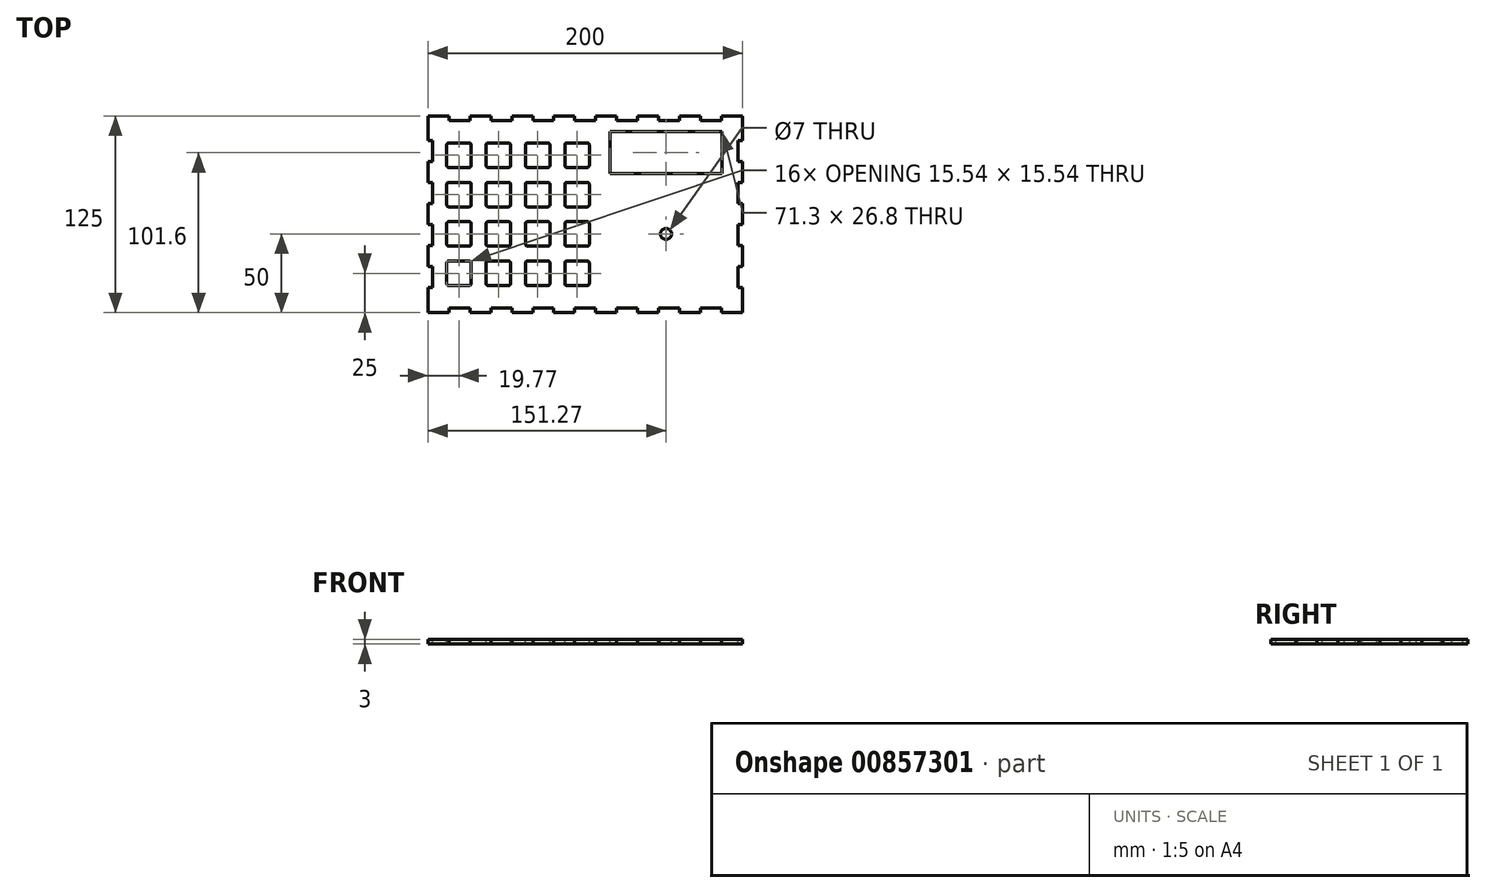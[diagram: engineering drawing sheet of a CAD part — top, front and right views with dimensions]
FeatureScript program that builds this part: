
annotation { "Feature Type Name" : "Feature", "Feature Type Description" : "" }
export const myFeature = defineFeature(function(context is Context, id is Id, definition is map)
    precondition{}
    {
        {
            var Q0;
            Q0=qCreatedBy(makeId("Top.planeOp"),FACE);
            var sketch = newSketch(context, id + "F0", { "sketchPlane" : qUnion([Q0])});
            skLineSegment(sketch, "E0.bottom", {"start": v(100, -62.5) * mm, "end": v(-100, -62.5) * mm});
            skLineSegment(sketch, "E0.top", {"start": v(100, 62.5) * mm, "end": v(-100, 62.5) * mm});
            skLineSegment(sketch, "E0.left", {"start": v(100, -62.5) * mm, "end": v(100, 62.5) * mm});
            skLineSegment(sketch, "E0.right", {"start": v(-100, -62.5) * mm, "end": v(-100, 62.5) * mm});
            skPoint(sketch, "E0.middle", {"position": v(0, 0) * mm});
            skSolve(sketch);
        }
        {
            var Q0;
            Q0=makeQuery(id+"F0.imprint","IMPRINT",FACE,{"disambiguationData":[TD([[makeQuery(id+"F0.imprint","IMPRINT",EDGE,{"derivedFrom":sQuery(id+"F0.wireOp",EDGE,"E0.bottom")}),-1.0]])]});
            extrude(context, id + "F1", {"entities" : qUnion([Q0]), "depth" : 3 * mm, "offsetDistance" : 25 * mm});
        }
        {
            var Q0;
            Q0=makeQuery(id+"F1.opExtrude","CAP_FACE",FACE,{"disambiguationData":[OSD([sQuery(id+"F0.wireOp",EDGE,"E0.bottom"),sQuery(id+"F0.wireOp",EDGE,"E0.top"),sQuery(id+"F0.wireOp",EDGE,"E0.left"),sQuery(id+"F0.wireOp",EDGE,"E0.right")])],"isStart":false});
            var sketch = newSketch(context, id + "F2", { "sketchPlane" : qUnion([Q0])});
            skLineSegment(sketch, "E1.bottom", {"start": v(-73.7, -45.27) * mm, "end": v(-86.75, -45.27) * mm});
            skLineSegment(sketch, "E1.top", {"start": v(-73.7, -29.73) * mm, "end": v(-86.75, -29.73) * mm});
            skLineSegment(sketch, "E1.left", {"start": v(-72.46, -44.02) * mm, "end": v(-72.46, -30.98) * mm});
            skLineSegment(sketch, "E1.right", {"start": v(-88, -44.02) * mm, "end": v(-88, -30.98) * mm});
            skPoint(sketch, "E1.middle", {"position": v(-80.23, -37.5) * mm});
            skPoint(sketch, "E2.visualSharp", {"position": v(-88, -29.73) * mm});
            skArc(sketch, "E2.filletArc", {"start": v(-86.75, -29.73) * mm, "mid": v(-87.63, -30.1) * mm, "end": v(-88, -30.98) * mm});
            skPoint(sketch, "E3.visualSharp", {"position": v(-72.46, -29.73) * mm});
            skArc(sketch, "E3.filletArc", {"start": v(-72.46, -30.98) * mm, "mid": v(-72.83, -30.1) * mm, "end": v(-73.7, -29.73) * mm});
            skPoint(sketch, "E4.visualSharp", {"position": v(-72.46, -45.27) * mm});
            skArc(sketch, "E4.filletArc", {"start": v(-73.7, -45.27) * mm, "mid": v(-72.83, -44.9) * mm, "end": v(-72.46, -44.02) * mm});
            skPoint(sketch, "E5.visualSharp", {"position": v(-88, -45.27) * mm});
            skArc(sketch, "E5.filletArc", {"start": v(-88, -44.02) * mm, "mid": v(-87.63, -44.9) * mm, "end": v(-86.75, -45.27) * mm});
            skLineSegment(sketch, "E6.0.1.0", {"start": v(-73.7, -4.73) * mm, "end": v(-86.75, -4.73) * mm});
            skPoint(sketch, "E6.0.1.1", {"position": v(-80.23, -12.5) * mm});
            skPoint(sketch, "E6.0.1.2", {"position": v(-72.46, -4.73) * mm});
            skLineSegment(sketch, "E6.0.1.3", {"start": v(-72.46, -19.02) * mm, "end": v(-72.46, -5.98) * mm});
            skLineSegment(sketch, "E6.0.1.4", {"start": v(-88, -19.02) * mm, "end": v(-88, -5.98) * mm});
            skPoint(sketch, "E6.0.1.5", {"position": v(-72.46, -20.27) * mm});
            skLineSegment(sketch, "E6.0.1.6", {"start": v(-73.7, -20.27) * mm, "end": v(-86.75, -20.27) * mm});
            skPoint(sketch, "E6.0.1.7", {"position": v(-88, -20.27) * mm});
            skPoint(sketch, "E6.0.1.8", {"position": v(-88, -4.73) * mm});
            skArc(sketch, "E6.0.1.9", {"start": v(-73.7, -20.27) * mm, "mid": v(-72.83, -19.9) * mm, "end": v(-72.46, -19.02) * mm});
            skArc(sketch, "E6.0.1.10", {"start": v(-88, -19.02) * mm, "mid": v(-87.63, -19.9) * mm, "end": v(-86.75, -20.27) * mm});
            skArc(sketch, "E6.0.1.11", {"start": v(-86.75, -4.73) * mm, "mid": v(-87.63, -5.1) * mm, "end": v(-88, -5.98) * mm});
            skArc(sketch, "E6.0.1.12", {"start": v(-72.46, -5.98) * mm, "mid": v(-72.83, -5.1) * mm, "end": v(-73.7, -4.73) * mm});
            skLineSegment(sketch, "E6.0.2.0", {"start": v(-73.7, 20.27) * mm, "end": v(-86.75, 20.27) * mm});
            skPoint(sketch, "E6.0.2.1", {"position": v(-80.23, 12.5) * mm});
            skPoint(sketch, "E6.0.2.2", {"position": v(-72.46, 20.27) * mm});
            skLineSegment(sketch, "E6.0.2.3", {"start": v(-72.46, 5.98) * mm, "end": v(-72.46, 19.02) * mm});
            skLineSegment(sketch, "E6.0.2.4", {"start": v(-88, 5.98) * mm, "end": v(-88, 19.02) * mm});
            skPoint(sketch, "E6.0.2.5", {"position": v(-72.46, 4.73) * mm});
            skLineSegment(sketch, "E6.0.2.6", {"start": v(-73.7, 4.73) * mm, "end": v(-86.75, 4.73) * mm});
            skPoint(sketch, "E6.0.2.7", {"position": v(-88, 4.73) * mm});
            skPoint(sketch, "E6.0.2.8", {"position": v(-88, 20.27) * mm});
            skArc(sketch, "E6.0.2.9", {"start": v(-73.7, 4.73) * mm, "mid": v(-72.83, 5.1) * mm, "end": v(-72.46, 5.98) * mm});
            skArc(sketch, "E6.0.2.10", {"start": v(-88, 5.98) * mm, "mid": v(-87.63, 5.1) * mm, "end": v(-86.75, 4.73) * mm});
            skArc(sketch, "E6.0.2.11", {"start": v(-86.75, 20.27) * mm, "mid": v(-87.63, 19.9) * mm, "end": v(-88, 19.02) * mm});
            skArc(sketch, "E6.0.2.12", {"start": v(-72.46, 19.02) * mm, "mid": v(-72.83, 19.9) * mm, "end": v(-73.7, 20.27) * mm});
            skLineSegment(sketch, "E6.0.3.0", {"start": v(-73.71, 45.27) * mm, "end": v(-86.75, 45.27) * mm});
            skPoint(sketch, "E6.0.3.1", {"position": v(-80.23, 37.5) * mm});
            skPoint(sketch, "E6.0.3.2", {"position": v(-72.46, 45.27) * mm});
            skLineSegment(sketch, "E6.0.3.3", {"start": v(-72.46, 30.98) * mm, "end": v(-72.46, 44.02) * mm});
            skLineSegment(sketch, "E6.0.3.4", {"start": v(-88, 30.98) * mm, "end": v(-88, 44.02) * mm});
            skPoint(sketch, "E6.0.3.5", {"position": v(-72.46, 29.73) * mm});
            skLineSegment(sketch, "E6.0.3.6", {"start": v(-73.71, 29.73) * mm, "end": v(-86.75, 29.73) * mm});
            skPoint(sketch, "E6.0.3.7", {"position": v(-88, 29.73) * mm});
            skPoint(sketch, "E6.0.3.8", {"position": v(-88, 45.27) * mm});
            skArc(sketch, "E6.0.3.9", {"start": v(-73.71, 29.73) * mm, "mid": v(-72.83, 30.1) * mm, "end": v(-72.46, 30.98) * mm});
            skArc(sketch, "E6.0.3.10", {"start": v(-88, 30.98) * mm, "mid": v(-87.63, 30.1) * mm, "end": v(-86.75, 29.73) * mm});
            skArc(sketch, "E6.0.3.11", {"start": v(-86.75, 45.27) * mm, "mid": v(-87.63, 44.9) * mm, "end": v(-88, 44.02) * mm});
            skArc(sketch, "E6.0.3.12", {"start": v(-72.46, 44.02) * mm, "mid": v(-72.83, 44.9) * mm, "end": v(-73.71, 45.27) * mm});
            skLineSegment(sketch, "E6.1.0.0", {"start": v(-48.71, -29.73) * mm, "end": v(-61.75, -29.73) * mm});
            skPoint(sketch, "E6.1.0.1", {"position": v(-55.23, -37.5) * mm});
            skPoint(sketch, "E6.1.0.2", {"position": v(-47.46, -29.73) * mm});
            skLineSegment(sketch, "E6.1.0.3", {"start": v(-47.46, -44.02) * mm, "end": v(-47.46, -30.98) * mm});
            skLineSegment(sketch, "E6.1.0.4", {"start": v(-63, -44.02) * mm, "end": v(-63, -30.98) * mm});
            skPoint(sketch, "E6.1.0.5", {"position": v(-47.46, -45.27) * mm});
            skLineSegment(sketch, "E6.1.0.6", {"start": v(-48.71, -45.27) * mm, "end": v(-61.75, -45.27) * mm});
            skPoint(sketch, "E6.1.0.7", {"position": v(-63, -45.27) * mm});
            skPoint(sketch, "E6.1.0.8", {"position": v(-63, -29.73) * mm});
            skArc(sketch, "E6.1.0.9", {"start": v(-48.71, -45.27) * mm, "mid": v(-47.83, -44.9) * mm, "end": v(-47.46, -44.02) * mm});
            skArc(sketch, "E6.1.0.10", {"start": v(-63, -44.02) * mm, "mid": v(-62.63, -44.9) * mm, "end": v(-61.75, -45.27) * mm});
            skArc(sketch, "E6.1.0.11", {"start": v(-61.75, -29.73) * mm, "mid": v(-62.63, -30.1) * mm, "end": v(-63, -30.98) * mm});
            skArc(sketch, "E6.1.0.12", {"start": v(-47.46, -30.98) * mm, "mid": v(-47.83, -30.1) * mm, "end": v(-48.71, -29.73) * mm});
            skLineSegment(sketch, "E6.1.1.0", {"start": v(-48.71, -4.73) * mm, "end": v(-61.75, -4.73) * mm});
            skPoint(sketch, "E6.1.1.1", {"position": v(-55.23, -12.5) * mm});
            skPoint(sketch, "E6.1.1.2", {"position": v(-47.46, -4.73) * mm});
            skLineSegment(sketch, "E6.1.1.3", {"start": v(-47.46, -19.02) * mm, "end": v(-47.46, -5.98) * mm});
            skLineSegment(sketch, "E6.1.1.4", {"start": v(-63, -19.02) * mm, "end": v(-63, -5.98) * mm});
            skPoint(sketch, "E6.1.1.5", {"position": v(-47.46, -20.27) * mm});
            skLineSegment(sketch, "E6.1.1.6", {"start": v(-48.71, -20.27) * mm, "end": v(-61.75, -20.27) * mm});
            skPoint(sketch, "E6.1.1.7", {"position": v(-63, -20.27) * mm});
            skPoint(sketch, "E6.1.1.8", {"position": v(-63, -4.73) * mm});
            skArc(sketch, "E6.1.1.9", {"start": v(-48.71, -20.27) * mm, "mid": v(-47.83, -19.9) * mm, "end": v(-47.46, -19.02) * mm});
            skArc(sketch, "E6.1.1.10", {"start": v(-63, -19.02) * mm, "mid": v(-62.63, -19.9) * mm, "end": v(-61.75, -20.27) * mm});
            skArc(sketch, "E6.1.1.11", {"start": v(-61.75, -4.73) * mm, "mid": v(-62.63, -5.1) * mm, "end": v(-63, -5.98) * mm});
            skArc(sketch, "E6.1.1.12", {"start": v(-47.46, -5.98) * mm, "mid": v(-47.83, -5.1) * mm, "end": v(-48.71, -4.73) * mm});
            skLineSegment(sketch, "E6.1.2.0", {"start": v(-48.71, 20.27) * mm, "end": v(-61.75, 20.27) * mm});
            skPoint(sketch, "E6.1.2.1", {"position": v(-55.23, 12.5) * mm});
            skPoint(sketch, "E6.1.2.2", {"position": v(-47.46, 20.27) * mm});
            skLineSegment(sketch, "E6.1.2.3", {"start": v(-47.46, 5.98) * mm, "end": v(-47.46, 19.02) * mm});
            skLineSegment(sketch, "E6.1.2.4", {"start": v(-63, 5.98) * mm, "end": v(-63, 19.02) * mm});
            skPoint(sketch, "E6.1.2.5", {"position": v(-47.46, 4.73) * mm});
            skLineSegment(sketch, "E6.1.2.6", {"start": v(-48.71, 4.73) * mm, "end": v(-61.75, 4.73) * mm});
            skPoint(sketch, "E6.1.2.7", {"position": v(-63, 4.73) * mm});
            skPoint(sketch, "E6.1.2.8", {"position": v(-63, 20.27) * mm});
            skArc(sketch, "E6.1.2.9", {"start": v(-48.71, 4.73) * mm, "mid": v(-47.83, 5.1) * mm, "end": v(-47.46, 5.98) * mm});
            skArc(sketch, "E6.1.2.10", {"start": v(-63, 5.98) * mm, "mid": v(-62.63, 5.1) * mm, "end": v(-61.75, 4.73) * mm});
            skArc(sketch, "E6.1.2.11", {"start": v(-61.75, 20.27) * mm, "mid": v(-62.63, 19.9) * mm, "end": v(-63, 19.02) * mm});
            skArc(sketch, "E6.1.2.12", {"start": v(-47.46, 19.02) * mm, "mid": v(-47.83, 19.9) * mm, "end": v(-48.71, 20.27) * mm});
            skLineSegment(sketch, "E6.1.3.0", {"start": v(-48.71, 45.27) * mm, "end": v(-61.75, 45.27) * mm});
            skPoint(sketch, "E6.1.3.1", {"position": v(-55.23, 37.5) * mm});
            skPoint(sketch, "E6.1.3.2", {"position": v(-47.46, 45.27) * mm});
            skLineSegment(sketch, "E6.1.3.3", {"start": v(-47.46, 30.98) * mm, "end": v(-47.46, 44.02) * mm});
            skLineSegment(sketch, "E6.1.3.4", {"start": v(-63, 30.98) * mm, "end": v(-63, 44.02) * mm});
            skPoint(sketch, "E6.1.3.5", {"position": v(-47.46, 29.73) * mm});
            skLineSegment(sketch, "E6.1.3.6", {"start": v(-48.71, 29.73) * mm, "end": v(-61.75, 29.73) * mm});
            skPoint(sketch, "E6.1.3.7", {"position": v(-63, 29.73) * mm});
            skPoint(sketch, "E6.1.3.8", {"position": v(-63, 45.27) * mm});
            skArc(sketch, "E6.1.3.9", {"start": v(-48.71, 29.73) * mm, "mid": v(-47.83, 30.1) * mm, "end": v(-47.46, 30.98) * mm});
            skArc(sketch, "E6.1.3.10", {"start": v(-63, 30.98) * mm, "mid": v(-62.63, 30.1) * mm, "end": v(-61.75, 29.73) * mm});
            skArc(sketch, "E6.1.3.11", {"start": v(-61.75, 45.27) * mm, "mid": v(-62.63, 44.9) * mm, "end": v(-63, 44.02) * mm});
            skArc(sketch, "E6.1.3.12", {"start": v(-47.46, 44.02) * mm, "mid": v(-47.83, 44.9) * mm, "end": v(-48.71, 45.27) * mm});
            skLineSegment(sketch, "E6.2.0.0", {"start": v(-23.71, -29.73) * mm, "end": v(-36.75, -29.73) * mm});
            skPoint(sketch, "E6.2.0.1", {"position": v(-30.23, -37.5) * mm});
            skPoint(sketch, "E6.2.0.2", {"position": v(-22.46, -29.73) * mm});
            skLineSegment(sketch, "E6.2.0.3", {"start": v(-22.46, -44.02) * mm, "end": v(-22.46, -30.98) * mm});
            skLineSegment(sketch, "E6.2.0.4", {"start": v(-38, -44.02) * mm, "end": v(-38, -30.98) * mm});
            skPoint(sketch, "E6.2.0.5", {"position": v(-22.46, -45.27) * mm});
            skLineSegment(sketch, "E6.2.0.6", {"start": v(-23.71, -45.27) * mm, "end": v(-36.75, -45.27) * mm});
            skPoint(sketch, "E6.2.0.7", {"position": v(-38, -45.27) * mm});
            skPoint(sketch, "E6.2.0.8", {"position": v(-38, -29.73) * mm});
            skArc(sketch, "E6.2.0.9", {"start": v(-23.71, -45.27) * mm, "mid": v(-22.83, -44.9) * mm, "end": v(-22.46, -44.02) * mm});
            skArc(sketch, "E6.2.0.10", {"start": v(-38, -44.02) * mm, "mid": v(-37.63, -44.9) * mm, "end": v(-36.75, -45.27) * mm});
            skArc(sketch, "E6.2.0.11", {"start": v(-36.75, -29.73) * mm, "mid": v(-37.63, -30.1) * mm, "end": v(-38, -30.98) * mm});
            skArc(sketch, "E6.2.0.12", {"start": v(-22.46, -30.98) * mm, "mid": v(-22.83, -30.1) * mm, "end": v(-23.71, -29.73) * mm});
            skLineSegment(sketch, "E6.2.1.0", {"start": v(-23.71, -4.73) * mm, "end": v(-36.75, -4.73) * mm});
            skPoint(sketch, "E6.2.1.1", {"position": v(-30.23, -12.5) * mm});
            skPoint(sketch, "E6.2.1.2", {"position": v(-22.46, -4.73) * mm});
            skLineSegment(sketch, "E6.2.1.3", {"start": v(-22.46, -19.02) * mm, "end": v(-22.46, -5.98) * mm});
            skLineSegment(sketch, "E6.2.1.4", {"start": v(-38, -19.02) * mm, "end": v(-38, -5.98) * mm});
            skPoint(sketch, "E6.2.1.5", {"position": v(-22.46, -20.27) * mm});
            skLineSegment(sketch, "E6.2.1.6", {"start": v(-23.71, -20.27) * mm, "end": v(-36.75, -20.27) * mm});
            skPoint(sketch, "E6.2.1.7", {"position": v(-38, -20.27) * mm});
            skPoint(sketch, "E6.2.1.8", {"position": v(-38, -4.73) * mm});
            skArc(sketch, "E6.2.1.9", {"start": v(-23.71, -20.27) * mm, "mid": v(-22.83, -19.9) * mm, "end": v(-22.46, -19.02) * mm});
            skArc(sketch, "E6.2.1.10", {"start": v(-38, -19.02) * mm, "mid": v(-37.63, -19.9) * mm, "end": v(-36.75, -20.27) * mm});
            skArc(sketch, "E6.2.1.11", {"start": v(-36.75, -4.73) * mm, "mid": v(-37.63, -5.1) * mm, "end": v(-38, -5.98) * mm});
            skArc(sketch, "E6.2.1.12", {"start": v(-22.46, -5.98) * mm, "mid": v(-22.83, -5.1) * mm, "end": v(-23.71, -4.73) * mm});
            skLineSegment(sketch, "E6.2.2.0", {"start": v(-23.71, 20.27) * mm, "end": v(-36.75, 20.27) * mm});
            skPoint(sketch, "E6.2.2.1", {"position": v(-30.23, 12.5) * mm});
            skPoint(sketch, "E6.2.2.2", {"position": v(-22.46, 20.27) * mm});
            skLineSegment(sketch, "E6.2.2.3", {"start": v(-22.46, 5.98) * mm, "end": v(-22.46, 19.02) * mm});
            skLineSegment(sketch, "E6.2.2.4", {"start": v(-38, 5.98) * mm, "end": v(-38, 19.02) * mm});
            skPoint(sketch, "E6.2.2.5", {"position": v(-22.46, 4.73) * mm});
            skLineSegment(sketch, "E6.2.2.6", {"start": v(-23.71, 4.73) * mm, "end": v(-36.75, 4.73) * mm});
            skPoint(sketch, "E6.2.2.7", {"position": v(-38, 4.73) * mm});
            skPoint(sketch, "E6.2.2.8", {"position": v(-38, 20.27) * mm});
            skArc(sketch, "E6.2.2.9", {"start": v(-23.71, 4.73) * mm, "mid": v(-22.83, 5.1) * mm, "end": v(-22.46, 5.98) * mm});
            skArc(sketch, "E6.2.2.10", {"start": v(-38, 5.98) * mm, "mid": v(-37.63, 5.1) * mm, "end": v(-36.75, 4.73) * mm});
            skArc(sketch, "E6.2.2.11", {"start": v(-36.75, 20.27) * mm, "mid": v(-37.63, 19.9) * mm, "end": v(-38, 19.02) * mm});
            skArc(sketch, "E6.2.2.12", {"start": v(-22.46, 19.02) * mm, "mid": v(-22.83, 19.9) * mm, "end": v(-23.71, 20.27) * mm});
            skLineSegment(sketch, "E6.2.3.0", {"start": v(-23.71, 45.27) * mm, "end": v(-36.75, 45.27) * mm});
            skPoint(sketch, "E6.2.3.1", {"position": v(-30.23, 37.5) * mm});
            skPoint(sketch, "E6.2.3.2", {"position": v(-22.46, 45.27) * mm});
            skLineSegment(sketch, "E6.2.3.3", {"start": v(-22.46, 30.98) * mm, "end": v(-22.46, 44.02) * mm});
            skLineSegment(sketch, "E6.2.3.4", {"start": v(-38, 30.98) * mm, "end": v(-38, 44.02) * mm});
            skPoint(sketch, "E6.2.3.5", {"position": v(-22.46, 29.73) * mm});
            skLineSegment(sketch, "E6.2.3.6", {"start": v(-23.71, 29.73) * mm, "end": v(-36.75, 29.73) * mm});
            skPoint(sketch, "E6.2.3.7", {"position": v(-38, 29.73) * mm});
            skPoint(sketch, "E6.2.3.8", {"position": v(-38, 45.27) * mm});
            skArc(sketch, "E6.2.3.9", {"start": v(-23.71, 29.73) * mm, "mid": v(-22.83, 30.1) * mm, "end": v(-22.46, 30.98) * mm});
            skArc(sketch, "E6.2.3.10", {"start": v(-38, 30.98) * mm, "mid": v(-37.63, 30.1) * mm, "end": v(-36.75, 29.73) * mm});
            skArc(sketch, "E6.2.3.11", {"start": v(-36.75, 45.27) * mm, "mid": v(-37.63, 44.9) * mm, "end": v(-38, 44.02) * mm});
            skArc(sketch, "E6.2.3.12", {"start": v(-22.46, 44.02) * mm, "mid": v(-22.83, 44.9) * mm, "end": v(-23.71, 45.27) * mm});
            skLineSegment(sketch, "E6.3.0.0", {"start": v(1.29, -29.73) * mm, "end": v(-11.75, -29.73) * mm});
            skPoint(sketch, "E6.3.0.1", {"position": v(-5.23, -37.5) * mm});
            skPoint(sketch, "E6.3.0.2", {"position": v(2.54, -29.73) * mm});
            skLineSegment(sketch, "E6.3.0.3", {"start": v(2.54, -44.02) * mm, "end": v(2.54, -30.98) * mm});
            skLineSegment(sketch, "E6.3.0.4", {"start": v(-13, -44.02) * mm, "end": v(-13, -30.98) * mm});
            skPoint(sketch, "E6.3.0.5", {"position": v(2.54, -45.27) * mm});
            skLineSegment(sketch, "E6.3.0.6", {"start": v(1.29, -45.27) * mm, "end": v(-11.75, -45.27) * mm});
            skPoint(sketch, "E6.3.0.7", {"position": v(-13, -45.27) * mm});
            skPoint(sketch, "E6.3.0.8", {"position": v(-13, -29.73) * mm});
            skArc(sketch, "E6.3.0.9", {"start": v(1.29, -45.27) * mm, "mid": v(2.17, -44.9) * mm, "end": v(2.54, -44.02) * mm});
            skArc(sketch, "E6.3.0.10", {"start": v(-13, -44.02) * mm, "mid": v(-12.63, -44.9) * mm, "end": v(-11.75, -45.27) * mm});
            skArc(sketch, "E6.3.0.11", {"start": v(-11.75, -29.73) * mm, "mid": v(-12.63, -30.1) * mm, "end": v(-13, -30.98) * mm});
            skArc(sketch, "E6.3.0.12", {"start": v(2.54, -30.98) * mm, "mid": v(2.17, -30.1) * mm, "end": v(1.29, -29.73) * mm});
            skLineSegment(sketch, "E6.3.1.0", {"start": v(1.29, -4.73) * mm, "end": v(-11.75, -4.73) * mm});
            skPoint(sketch, "E6.3.1.1", {"position": v(-5.23, -12.5) * mm});
            skPoint(sketch, "E6.3.1.2", {"position": v(2.54, -4.73) * mm});
            skLineSegment(sketch, "E6.3.1.3", {"start": v(2.54, -19.02) * mm, "end": v(2.54, -5.98) * mm});
            skLineSegment(sketch, "E6.3.1.4", {"start": v(-13, -19.02) * mm, "end": v(-13, -5.98) * mm});
            skPoint(sketch, "E6.3.1.5", {"position": v(2.54, -20.27) * mm});
            skLineSegment(sketch, "E6.3.1.6", {"start": v(1.29, -20.27) * mm, "end": v(-11.75, -20.27) * mm});
            skPoint(sketch, "E6.3.1.7", {"position": v(-13, -20.27) * mm});
            skPoint(sketch, "E6.3.1.8", {"position": v(-13, -4.73) * mm});
            skArc(sketch, "E6.3.1.9", {"start": v(1.29, -20.27) * mm, "mid": v(2.17, -19.9) * mm, "end": v(2.54, -19.02) * mm});
            skArc(sketch, "E6.3.1.10", {"start": v(-13, -19.02) * mm, "mid": v(-12.63, -19.9) * mm, "end": v(-11.75, -20.27) * mm});
            skArc(sketch, "E6.3.1.11", {"start": v(-11.75, -4.73) * mm, "mid": v(-12.63, -5.1) * mm, "end": v(-13, -5.98) * mm});
            skArc(sketch, "E6.3.1.12", {"start": v(2.54, -5.98) * mm, "mid": v(2.17, -5.1) * mm, "end": v(1.29, -4.73) * mm});
            skLineSegment(sketch, "E6.3.2.0", {"start": v(1.29, 20.27) * mm, "end": v(-11.75, 20.27) * mm});
            skPoint(sketch, "E6.3.2.1", {"position": v(-5.23, 12.5) * mm});
            skPoint(sketch, "E6.3.2.2", {"position": v(2.54, 20.27) * mm});
            skLineSegment(sketch, "E6.3.2.3", {"start": v(2.54, 5.98) * mm, "end": v(2.54, 19.02) * mm});
            skLineSegment(sketch, "E6.3.2.4", {"start": v(-13, 5.98) * mm, "end": v(-13, 19.02) * mm});
            skPoint(sketch, "E6.3.2.5", {"position": v(2.54, 4.73) * mm});
            skLineSegment(sketch, "E6.3.2.6", {"start": v(1.29, 4.73) * mm, "end": v(-11.75, 4.73) * mm});
            skPoint(sketch, "E6.3.2.7", {"position": v(-13, 4.73) * mm});
            skPoint(sketch, "E6.3.2.8", {"position": v(-13, 20.27) * mm});
            skArc(sketch, "E6.3.2.9", {"start": v(1.29, 4.73) * mm, "mid": v(2.17, 5.1) * mm, "end": v(2.54, 5.98) * mm});
            skArc(sketch, "E6.3.2.10", {"start": v(-13, 5.98) * mm, "mid": v(-12.63, 5.1) * mm, "end": v(-11.75, 4.73) * mm});
            skArc(sketch, "E6.3.2.11", {"start": v(-11.75, 20.27) * mm, "mid": v(-12.63, 19.9) * mm, "end": v(-13, 19.02) * mm});
            skArc(sketch, "E6.3.2.12", {"start": v(2.54, 19.02) * mm, "mid": v(2.17, 19.9) * mm, "end": v(1.29, 20.27) * mm});
            skLineSegment(sketch, "E6.3.3.0", {"start": v(1.29, 45.27) * mm, "end": v(-11.75, 45.27) * mm});
            skPoint(sketch, "E6.3.3.1", {"position": v(-5.23, 37.5) * mm});
            skPoint(sketch, "E6.3.3.2", {"position": v(2.54, 45.27) * mm});
            skLineSegment(sketch, "E6.3.3.3", {"start": v(2.54, 30.98) * mm, "end": v(2.54, 44.02) * mm});
            skLineSegment(sketch, "E6.3.3.4", {"start": v(-13, 30.98) * mm, "end": v(-13, 44.02) * mm});
            skPoint(sketch, "E6.3.3.5", {"position": v(2.54, 29.73) * mm});
            skLineSegment(sketch, "E6.3.3.6", {"start": v(1.29, 29.73) * mm, "end": v(-11.75, 29.73) * mm});
            skPoint(sketch, "E6.3.3.7", {"position": v(-13, 29.73) * mm});
            skPoint(sketch, "E6.3.3.8", {"position": v(-13, 45.27) * mm});
            skArc(sketch, "E6.3.3.9", {"start": v(1.29, 29.73) * mm, "mid": v(2.17, 30.1) * mm, "end": v(2.54, 30.98) * mm});
            skArc(sketch, "E6.3.3.10", {"start": v(-13, 30.98) * mm, "mid": v(-12.63, 30.1) * mm, "end": v(-11.75, 29.73) * mm});
            skArc(sketch, "E6.3.3.11", {"start": v(-11.75, 45.27) * mm, "mid": v(-12.63, 44.9) * mm, "end": v(-13, 44.02) * mm});
            skArc(sketch, "E6.3.3.12", {"start": v(2.54, 44.02) * mm, "mid": v(2.17, 44.9) * mm, "end": v(1.29, 45.27) * mm});
            skLineSegment(sketch, "E6.direction1", {"start": v(-88, -45.27) * mm, "end": v(-63, -45.27) * mm, "construction": true});
            skLineSegment(sketch, "E6.direction2", {"start": v(-88, -45.27) * mm, "end": v(-88, -20.27) * mm, "construction": true});
            skSolve(sketch);
        }
        {
            var Q0;
            Q0 = qSketchRegion(id + "F2", true);
            extrude(context, id + "F3", {"entities" : qUnion([Q0]), "operationType" : NewBodyOperationType.REMOVE, "endBound" : BoundingType.THROUGH_ALL, "oppositeDirection" : true, "depth" : 25 * mm, "offsetDistance" : 25 * mm});
        }
        {
            var Q0;
            Q0=makeQuery(id+"F1.opExtrude","CAP_FACE",FACE,{"disambiguationData":[OSD([sQuery(id+"F0.wireOp",EDGE,"E0.bottom"),sQuery(id+"F0.wireOp",EDGE,"E0.top"),sQuery(id+"F0.wireOp",EDGE,"E0.left"),sQuery(id+"F0.wireOp",EDGE,"E0.right")])],"isStart":false});
            var sketch = newSketch(context, id + "F4", { "sketchPlane" : qUnion([Q0])});
            skLineSegment(sketch, "E7", {"start": v(-100, -12.5) * mm, "end": v(100, -12.5) * mm, "construction": true});
            skPoint(sketch, "E8.startSnap0", {"position": v(2.54, 37.5) * mm});
            skCircle(sketch, "E9", {"center": v(51.27, -12.5) * mm, "radius": 3.5 * mm});
            skSolve(sketch);
        }
        {
            var Q0;
            Q0 = qSketchRegion(id + "F4", true);
            extrude(context, id + "F5", {"entities" : qUnion([Q0]), "operationType" : NewBodyOperationType.REMOVE, "endBound" : BoundingType.THROUGH_ALL, "oppositeDirection" : true, "depth" : 25 * mm, "offsetDistance" : 25 * mm});
        }
        {
            var Q0;
            Q0=makeQuery(id+"F1.opExtrude","CAP_FACE",FACE,{"disambiguationData":[OSD([sQuery(id+"F0.wireOp",EDGE,"E0.bottom"),sQuery(id+"F0.wireOp",EDGE,"E0.top"),sQuery(id+"F0.wireOp",EDGE,"E0.left"),sQuery(id+"F0.wireOp",EDGE,"E0.right")])],"isStart":false});
            var sketch = newSketch(context, id + "F6", { "sketchPlane" : qUnion([Q0])});
            skCircle(sketch, "E10", {"center": v(51.27, -12.5) * mm, "radius": 27.5 * mm, "construction": true});
            skLineSegment(sketch, "E11", {"start": v(51.27, -12.5) * mm, "end": v(51.27, 62.5) * mm, "construction": true});
            skLineSegment(sketch, "E12.bottom", {"start": v(86.92, 25.7) * mm, "end": v(15.62, 25.7) * mm});
            skLineSegment(sketch, "E12.top", {"start": v(86.92, 52.5) * mm, "end": v(15.62, 52.5) * mm});
            skLineSegment(sketch, "E12.left", {"start": v(86.92, 25.7) * mm, "end": v(86.92, 52.5) * mm});
            skLineSegment(sketch, "E12.right", {"start": v(15.62, 25.7) * mm, "end": v(15.62, 52.5) * mm});
            skPoint(sketch, "E12.middle", {"position": v(51.27, 39.1) * mm});
            skLineSegment(sketch, "E13", {"start": v(-47.83, 5.1) * mm, "end": v(-35.87, -6.86) * mm, "construction": true});
            skLineSegment(sketch, "E14.bottom", {"start": v(8.15, -50.88) * mm, "end": v(-91.85, -50.88) * mm, "construction": true});
            skLineSegment(sketch, "E14.top", {"start": v(8.15, 49.12) * mm, "end": v(-91.85, 49.12) * mm, "construction": true});
            skLineSegment(sketch, "E14.left", {"start": v(8.15, -50.88) * mm, "end": v(8.15, 49.12) * mm, "construction": true});
            skLineSegment(sketch, "E14.right", {"start": v(-91.85, -50.88) * mm, "end": v(-91.85, 49.12) * mm, "construction": true});
            skPoint(sketch, "E14.middle", {"position": v(-41.85, -0.88) * mm});
            skSolve(sketch);
        }
        {
            var Q0;
            Q0 = qSketchRegion(id + "F6", true);
            extrude(context, id + "F7", {"entities" : qUnion([Q0]), "operationType" : NewBodyOperationType.REMOVE, "endBound" : BoundingType.THROUGH_ALL, "oppositeDirection" : true, "depth" : 25 * mm, "offsetDistance" : 25 * mm});
        }
        {
            var Q0;
            Q0=makeQuery(id+"F1.opExtrude","CAP_FACE",FACE,{"disambiguationData":[OSD([sQuery(id+"F0.wireOp",EDGE,"E0.bottom"),sQuery(id+"F0.wireOp",EDGE,"E0.top"),sQuery(id+"F0.wireOp",EDGE,"E0.left"),sQuery(id+"F0.wireOp",EDGE,"E0.right")])],"isStart":false});
            var sketch = newSketch(context, id + "F8", { "sketchPlane" : qUnion([Q0])});
            skLineSegment(sketch, "E15.bottom", {"start": v(-86.67, 62.5) * mm, "end": v(-73.33, 62.5) * mm});
            skLineSegment(sketch, "E15.top", {"start": v(-86.67, 59.5) * mm, "end": v(-73.33, 59.5) * mm});
            skLineSegment(sketch, "E15.left", {"start": v(-86.67, 62.5) * mm, "end": v(-86.67, 59.5) * mm});
            skLineSegment(sketch, "E15.right", {"start": v(-73.33, 62.5) * mm, "end": v(-73.33, 59.5) * mm});
            skLineSegment(sketch, "E16.1.0.0", {"start": v(-60, 62.5) * mm, "end": v(-46.67, 62.5) * mm});
            skLineSegment(sketch, "E16.1.0.1", {"start": v(-60, 62.5) * mm, "end": v(-60, 59.5) * mm});
            skLineSegment(sketch, "E16.1.0.2", {"start": v(-46.67, 62.5) * mm, "end": v(-46.67, 59.5) * mm});
            skLineSegment(sketch, "E16.1.0.3", {"start": v(-60, 59.5) * mm, "end": v(-46.67, 59.5) * mm});
            skLineSegment(sketch, "E16.2.0.0", {"start": v(-33.33, 62.5) * mm, "end": v(-20, 62.5) * mm});
            skLineSegment(sketch, "E16.2.0.1", {"start": v(-33.33, 62.5) * mm, "end": v(-33.33, 59.5) * mm});
            skLineSegment(sketch, "E16.2.0.2", {"start": v(-20, 62.5) * mm, "end": v(-20, 59.5) * mm});
            skLineSegment(sketch, "E16.2.0.3", {"start": v(-33.33, 59.5) * mm, "end": v(-20, 59.5) * mm});
            skLineSegment(sketch, "E16.3.0.0", {"start": v(-6.67, 62.5) * mm, "end": v(6.67, 62.5) * mm});
            skLineSegment(sketch, "E16.3.0.1", {"start": v(-6.67, 62.5) * mm, "end": v(-6.67, 59.5) * mm});
            skLineSegment(sketch, "E16.3.0.2", {"start": v(6.67, 62.5) * mm, "end": v(6.67, 59.5) * mm});
            skLineSegment(sketch, "E16.3.0.3", {"start": v(-6.67, 59.5) * mm, "end": v(6.67, 59.5) * mm});
            skLineSegment(sketch, "E16.4.0.0", {"start": v(20, 62.5) * mm, "end": v(33.33, 62.5) * mm});
            skLineSegment(sketch, "E16.4.0.1", {"start": v(20, 62.5) * mm, "end": v(20, 59.5) * mm});
            skLineSegment(sketch, "E16.4.0.2", {"start": v(33.33, 62.5) * mm, "end": v(33.33, 59.5) * mm});
            skLineSegment(sketch, "E16.4.0.3", {"start": v(20, 59.5) * mm, "end": v(33.33, 59.5) * mm});
            skLineSegment(sketch, "E16.5.0.0", {"start": v(46.67, 62.5) * mm, "end": v(60, 62.5) * mm});
            skLineSegment(sketch, "E16.5.0.1", {"start": v(46.67, 62.5) * mm, "end": v(46.67, 59.5) * mm});
            skLineSegment(sketch, "E16.5.0.2", {"start": v(60, 62.5) * mm, "end": v(60, 59.5) * mm});
            skLineSegment(sketch, "E16.5.0.3", {"start": v(46.67, 59.5) * mm, "end": v(60, 59.5) * mm});
            skLineSegment(sketch, "E16.6.0.0", {"start": v(73.33, 62.5) * mm, "end": v(86.67, 62.5) * mm});
            skLineSegment(sketch, "E16.6.0.1", {"start": v(73.33, 62.5) * mm, "end": v(73.33, 59.5) * mm});
            skLineSegment(sketch, "E16.6.0.2", {"start": v(86.67, 62.5) * mm, "end": v(86.67, 59.5) * mm});
            skLineSegment(sketch, "E16.6.0.3", {"start": v(73.33, 59.5) * mm, "end": v(86.67, 59.5) * mm});
            skLineSegment(sketch, "E17.bottom", {"start": v(-100, 46.66) * mm, "end": v(-97, 46.66) * mm});
            skLineSegment(sketch, "E17.top", {"start": v(-100, 33.33) * mm, "end": v(-97, 33.33) * mm});
            skLineSegment(sketch, "E17.left", {"start": v(-100, 46.66) * mm, "end": v(-100, 33.33) * mm});
            skLineSegment(sketch, "E17.right", {"start": v(-97, 46.66) * mm, "end": v(-97, 33.33) * mm});
            skLineSegment(sketch, "E18.0.1.0", {"start": v(-100, 20) * mm, "end": v(-100, 6.67) * mm});
            skLineSegment(sketch, "E18.0.1.1", {"start": v(-97, 20) * mm, "end": v(-97, 6.67) * mm});
            skLineSegment(sketch, "E18.0.1.2", {"start": v(-100, 6.67) * mm, "end": v(-97, 6.67) * mm});
            skLineSegment(sketch, "E18.0.1.3", {"start": v(-100, 20) * mm, "end": v(-97, 20) * mm});
            skLineSegment(sketch, "E18.0.2.0", {"start": v(-100, -6.67) * mm, "end": v(-100, -20) * mm});
            skLineSegment(sketch, "E18.0.2.1", {"start": v(-97, -6.67) * mm, "end": v(-97, -20) * mm});
            skLineSegment(sketch, "E18.0.2.2", {"start": v(-100, -20) * mm, "end": v(-97, -20) * mm});
            skLineSegment(sketch, "E18.0.2.3", {"start": v(-100, -6.67) * mm, "end": v(-97, -6.67) * mm});
            skLineSegment(sketch, "E18.0.3.0", {"start": v(-100, -33.33) * mm, "end": v(-100, -46.67) * mm});
            skLineSegment(sketch, "E18.0.3.1", {"start": v(-97, -33.33) * mm, "end": v(-97, -46.67) * mm});
            skLineSegment(sketch, "E18.0.3.2", {"start": v(-100, -46.67) * mm, "end": v(-97, -46.67) * mm});
            skLineSegment(sketch, "E18.0.3.3", {"start": v(-100, -33.33) * mm, "end": v(-97, -33.33) * mm});
            skLineSegment(sketch, "E18.direction1", {"start": v(-100, 33.33) * mm, "end": v(-75, 33.33) * mm, "construction": true});
            skLineSegment(sketch, "E18.direction2", {"start": v(-100, 33.33) * mm, "end": v(-100, 6.67) * mm, "construction": true});
            skLineSegment(sketch, "E19", {"start": v(-100, 0) * mm, "end": v(100, 0) * mm, "construction": true});
            skLineSegment(sketch, "E20", {"start": v(0, 62.5) * mm, "end": v(0, -62.5) * mm, "construction": true});
            skLineSegment(sketch, "E21.MirrorCS", {"start": v(-86.67, -62.5) * mm, "end": v(-86.67, -59.5) * mm});
            skLineSegment(sketch, "E22.MirrorCS", {"start": v(-20, -62.5) * mm, "end": v(-20, -59.5) * mm});
            skLineSegment(sketch, "E23.MirrorCS", {"start": v(20, -62.5) * mm, "end": v(20, -59.5) * mm});
            skLineSegment(sketch, "E24.MirrorCS", {"start": v(-73.33, -62.5) * mm, "end": v(-73.33, -59.5) * mm});
            skLineSegment(sketch, "E25.MirrorCS", {"start": v(-60, -62.5) * mm, "end": v(-60, -59.5) * mm});
            skLineSegment(sketch, "E26.MirrorCS", {"start": v(-33.33, -62.5) * mm, "end": v(-33.33, -59.5) * mm});
            skLineSegment(sketch, "E27.MirrorCS", {"start": v(6.67, -62.5) * mm, "end": v(6.67, -59.5) * mm});
            skLineSegment(sketch, "E28.MirrorCS", {"start": v(46.67, -62.5) * mm, "end": v(46.67, -59.5) * mm});
            skLineSegment(sketch, "E29.MirrorCS", {"start": v(60, -62.5) * mm, "end": v(60, -59.5) * mm});
            skLineSegment(sketch, "E30.MirrorCS", {"start": v(73.33, -62.5) * mm, "end": v(73.33, -59.5) * mm});
            skLineSegment(sketch, "E31.MirrorCS", {"start": v(-6.67, -62.5) * mm, "end": v(-6.67, -59.5) * mm});
            skLineSegment(sketch, "E32.MirrorCS", {"start": v(-46.67, -62.5) * mm, "end": v(-46.67, -59.5) * mm});
            skLineSegment(sketch, "E33.MirrorCS", {"start": v(33.33, -62.5) * mm, "end": v(33.33, -59.5) * mm});
            skLineSegment(sketch, "E34.MirrorCS", {"start": v(86.67, -62.5) * mm, "end": v(86.67, -59.5) * mm});
            skLineSegment(sketch, "E35.MirrorCS", {"start": v(-33.33, -59.5) * mm, "end": v(-20, -59.5) * mm});
            skLineSegment(sketch, "E36.MirrorCS", {"start": v(73.33, -59.5) * mm, "end": v(86.67, -59.5) * mm});
            skLineSegment(sketch, "E37.MirrorCS", {"start": v(-60, -59.5) * mm, "end": v(-46.67, -59.5) * mm});
            skLineSegment(sketch, "E38.MirrorCS", {"start": v(20, -59.5) * mm, "end": v(33.33, -59.5) * mm});
            skLineSegment(sketch, "E39.MirrorCS", {"start": v(-86.67, -59.5) * mm, "end": v(-73.33, -59.5) * mm});
            skLineSegment(sketch, "E40.MirrorCS", {"start": v(46.67, -62.5) * mm, "end": v(60, -62.5) * mm});
            skLineSegment(sketch, "E41.MirrorCS", {"start": v(20, -62.5) * mm, "end": v(33.33, -62.5) * mm});
            skLineSegment(sketch, "E42.MirrorCS", {"start": v(-6.67, -62.5) * mm, "end": v(6.67, -62.5) * mm});
            skLineSegment(sketch, "E43.MirrorCS", {"start": v(73.33, -62.5) * mm, "end": v(86.67, -62.5) * mm});
            skLineSegment(sketch, "E44.MirrorCS", {"start": v(-33.33, -62.5) * mm, "end": v(-20, -62.5) * mm});
            skLineSegment(sketch, "E45.MirrorCS", {"start": v(46.67, -59.5) * mm, "end": v(60, -59.5) * mm});
            skLineSegment(sketch, "E46.MirrorCS", {"start": v(-86.67, -62.5) * mm, "end": v(-73.33, -62.5) * mm});
            skLineSegment(sketch, "E47.MirrorCS", {"start": v(-60, -62.5) * mm, "end": v(-46.67, -62.5) * mm});
            skLineSegment(sketch, "E48.MirrorCS", {"start": v(-6.67, -59.5) * mm, "end": v(6.67, -59.5) * mm});
            skLineSegment(sketch, "E49.MirrorCS", {"start": v(100, -20) * mm, "end": v(97, -20) * mm});
            skLineSegment(sketch, "E50.MirrorCS", {"start": v(100, 6.67) * mm, "end": v(97, 6.67) * mm});
            skLineSegment(sketch, "E51.MirrorCS", {"start": v(100, -33.33) * mm, "end": v(97, -33.33) * mm});
            skLineSegment(sketch, "E52.MirrorCS", {"start": v(100, -6.67) * mm, "end": v(97, -6.67) * mm});
            skLineSegment(sketch, "E53.MirrorCS", {"start": v(100, 33.33) * mm, "end": v(97, 33.33) * mm});
            skLineSegment(sketch, "E54.MirrorCS", {"start": v(100, 46.66) * mm, "end": v(97, 46.66) * mm});
            skLineSegment(sketch, "E55.MirrorCS", {"start": v(100, -46.67) * mm, "end": v(97, -46.67) * mm});
            skLineSegment(sketch, "E56.MirrorCS", {"start": v(100, 20) * mm, "end": v(97, 20) * mm});
            skLineSegment(sketch, "E57.MirrorCS", {"start": v(100, 20) * mm, "end": v(100, 6.67) * mm});
            skLineSegment(sketch, "E58.MirrorCS", {"start": v(97, -6.67) * mm, "end": v(97, -20) * mm});
            skLineSegment(sketch, "E59.MirrorCS", {"start": v(100, 33.33) * mm, "end": v(100, 6.67) * mm, "construction": true});
            skLineSegment(sketch, "E60.MirrorCS", {"start": v(100, -33.33) * mm, "end": v(100, -46.67) * mm});
            skLineSegment(sketch, "E61.MirrorCS", {"start": v(100, 46.66) * mm, "end": v(100, 33.33) * mm});
            skLineSegment(sketch, "E62.MirrorCS", {"start": v(100, -6.67) * mm, "end": v(100, -20) * mm});
            skLineSegment(sketch, "E63.MirrorCS", {"start": v(97, -33.33) * mm, "end": v(97, -46.67) * mm});
            skLineSegment(sketch, "E64.MirrorCS", {"start": v(97, 20) * mm, "end": v(97, 6.67) * mm});
            skLineSegment(sketch, "E65.MirrorCS", {"start": v(97, 46.66) * mm, "end": v(97, 33.33) * mm});
            skSolve(sketch);
        }
        {
            var Q0;
            Q0 = qSketchRegion(id + "F8", true);
            extrude(context, id + "F9", {"entities" : qUnion([Q0]), "operationType" : NewBodyOperationType.REMOVE, "endBound" : BoundingType.THROUGH_ALL, "oppositeDirection" : true, "depth" : 25 * mm, "offsetDistance" : 25 * mm});
        }
    });
